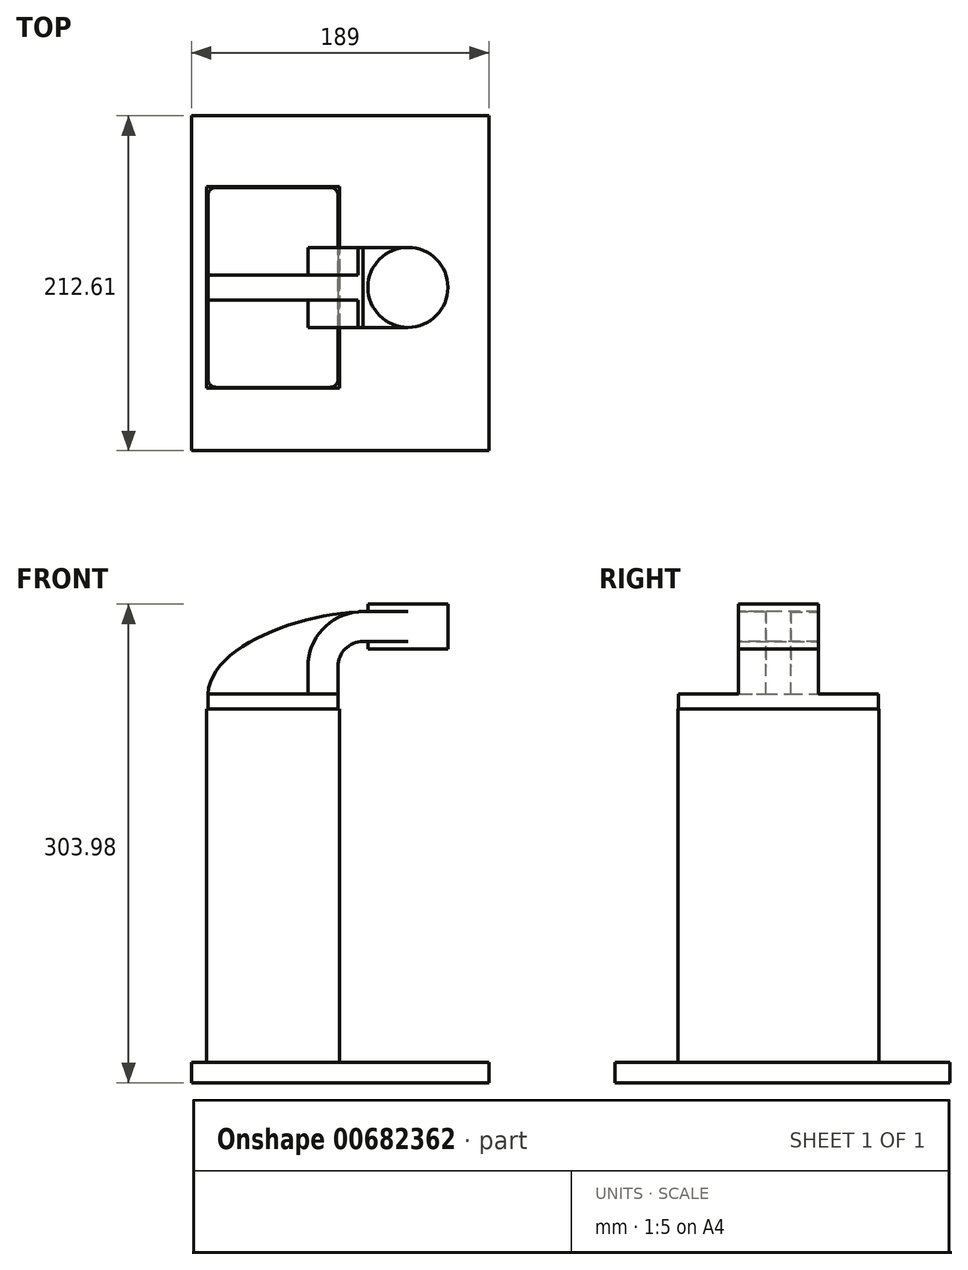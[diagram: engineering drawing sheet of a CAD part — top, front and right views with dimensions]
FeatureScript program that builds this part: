
annotation { "Feature Type Name" : "Feature", "Feature Type Description" : "" }
export const myFeature = defineFeature(function(context is Context, id is Id, definition is map)
    precondition{}
    {
        {
            var Q0;
            Q0=qCreatedBy(makeId("Front.planeOp"),FACE);
            var sketch = newSketch(context, id + "F0", { "sketchPlane" : qUnion([Q0])});
            skLineSegment(sketch, "E0.rect.bottom", {"start": v(-41.28, 9.52) * mm, "end": v(41.28, 9.52) * mm});
            skLineSegment(sketch, "E0.rect.top", {"start": v(-41.28, -9.52) * mm, "end": v(41.28, -9.52) * mm});
            skLineSegment(sketch, "E0.rect.left", {"start": v(-41.28, 9.52) * mm, "end": v(-41.28, -9.52) * mm});
            skLineSegment(sketch, "E0.rect.right", {"start": v(41.28, 9.52) * mm, "end": v(41.28, -9.52) * mm});
            skPoint(sketch, "E0.rect.middle", {"position": v(0, 0) * mm});
            skLineSegment(sketch, "E1", {"start": v(41.28, 9.52) * mm, "end": v(41.28, 27) * mm});
            skArc(sketch, "E2", {"start": v(41.28, 27) * mm, "mid": v(45.92, 38.23) * mm, "end": v(57.15, 42.88) * mm});
            skLineSegment(sketch, "E3", {"start": v(57.15, 42.88) * mm, "end": v(85.72, 42.88) * mm});
            skLineSegment(sketch, "E4.rect.bottom", {"start": v(60.32, 38.1) * mm, "end": v(111.12, 38.1) * mm});
            skLineSegment(sketch, "E4.rect.top", {"start": v(60.32, 66.68) * mm, "end": v(111.12, 66.68) * mm});
            skLineSegment(sketch, "E4.rect.left", {"start": v(60.32, 38.1) * mm, "end": v(60.32, 66.68) * mm});
            skLineSegment(sketch, "E4.rect.right", {"start": v(111.13, 38.1) * mm, "end": v(111.12, 66.68) * mm});
            skPoint(sketch, "E4.rect.middle", {"position": v(85.72, 52.39) * mm});
            skLineSegment(sketch, "E5.0", {"start": v(57.15, 61.93) * mm, "end": v(85.72, 61.93) * mm});
            skArc(sketch, "E5.1", {"start": v(22.23, 27) * mm, "mid": v(32.45, 51.7) * mm, "end": v(57.15, 61.93) * mm});
            skLineSegment(sketch, "E5.2", {"start": v(22.23, 9.52) * mm, "end": v(22.23, 27) * mm});
            skLineSegment(sketch, "E6", {"start": v(85.72, 38.1) * mm, "end": v(85.72, 66.68) * mm});
            skFitSpline(sketch, "E7", {"points": [v(-41.28, 9.53) * mm, v(57.15, 61.93) * mm], "startDerivative": vector(5.2, 92.34) * mm, "endDerivative": vector(120.92, 4.22) * mm});
            skSolve(sketch);
        }
        {
            var Q0;
            Q0=makeQuery(id+"F0.imprint","IMPRINT",FACE,{"disambiguationData":[TD([[makeQuery(id+"F0.imprint","IMPRINT",EDGE,{"derivedFrom":sQuery(id+"F0.wireOp",EDGE,"E0.rect.top")}),1.0]])]});
            extrude(context, id + "F1", {"entities" : qUnion([Q0]), "endBound" : BoundingType.SYMMETRIC, "depth" : 127 * mm});
        }
        {
            var Q0;
            {var subQ9=sQuery(id+"F0.wireOp",EDGE,"E1");Q0=makeQuery(id+"F0.imprint","IMPRINT",FACE,{"disambiguationData":[TD([[makeQuery(id+"F0.imprint","IMPRINT",EDGE,{"derivedFrom":subQ9}),1.0]])]});}
            var Q1;
            {var subQ0=sQuery(id+"F0.wireOp",EDGE,"E6");var subQ1=sQuery(id+"F0.wireOp",EDGE,"E3");var subQ2=makeQuery(id+"F0.imprint","INTERSECT",VERTEX,{"derivedFrom":[subQ1,subQ0]});Q1=makeQuery(id+"F0.imprint","IMPRINT",FACE,{"disambiguationData":[TD([[makeQuery(id+"F0.imprint","IMPRINT",EDGE,{"disambiguationData":[TD([[subQ2,1.0]])],"derivedFrom":subQ1}),1.0]])]});}
            extrude(context, id + "F2", {"entities" : qUnion([Q0, Q1]), "operationType" : NewBodyOperationType.ADD, "endBound" : BoundingType.SYMMETRIC, "depth" : 50.8 * mm});
        }
        {
            var Q0;
            {var subQ3=sQuery(id+"F0.wireOp",EDGE,"E5.2");Q0=makeQuery(id+"F0.imprint","IMPRINT",FACE,{"disambiguationData":[TD([[makeQuery(id+"F0.imprint","IMPRINT",EDGE,{"derivedFrom":subQ3}),1.0]])]});}
            extrude(context, id + "F3", {"entities" : qUnion([Q0]), "operationType" : NewBodyOperationType.ADD, "endBound" : BoundingType.SYMMETRIC, "depth" : 15.88 * mm});
        }
        {
            var Q0;
            {var subQ5=sQuery(id+"F0.wireOp",EDGE,"E4.rect.right");Q0=makeQuery(id+"F0.imprint","IMPRINT",FACE,{"disambiguationData":[TD([[makeQuery(id+"F0.imprint","IMPRINT",EDGE,{"derivedFrom":subQ5}),1.0]])]});}
            var Q1;
            Q1=sQuery(id+"F0.wireOp",EDGE,"E6");
            revolve(context, id + "F4", {"operationType" : NewBodyOperationType.ADD, "entities" : qUnion([Q0]), "axis" : qUnion([Q1]), "revolveType" : RevolveType.FULL});
        }
        {
            var Q0;
            Q0=makeQuery(id+"F1.opExtrude","CAP_EDGE",EDGE,{"disambiguationData":[OSD([sQuery(id+"F0.wireOp",EDGE,"E0.rect.right")])],"isStart":false});
            var Q1;
            Q1=makeQuery(id+"F1.opExtrude","CAP_EDGE",EDGE,{"disambiguationData":[OSD([sQuery(id+"F0.wireOp",EDGE,"E0.rect.left")])],"isStart":false});
            var Q2;
            Q2=makeQuery(id+"F1.opExtrude","CAP_EDGE",EDGE,{"disambiguationData":[OSD([sQuery(id+"F0.wireOp",EDGE,"E0.rect.right")])],"isStart":true});
            var Q3;
            Q3=makeQuery(id+"F1.opExtrude","CAP_EDGE",EDGE,{"disambiguationData":[OSD([sQuery(id+"F0.wireOp",EDGE,"E0.rect.left")])],"isStart":true});
            fillet(context, id + "F5", {"entities" : qUnion([Q0, Q1, Q2, Q3]), "radius" : 5.08 * mm, "tangentPropagation" : true, "allowEdgeOverflow" : false});
        }
        {
            var Q0;
            Q0=qCreatedBy(makeId("Top.planeOp"),FACE);
            var sketch = newSketch(context, id + "F6", { "sketchPlane" : qUnion([Q0])});
            skLineSegment(sketch, "E8.bottom", {"start": v(42.19, -63.88) * mm, "end": v(-42.19, -63.88) * mm});
            skLineSegment(sketch, "E8.top", {"start": v(42.19, 63.88) * mm, "end": v(-42.19, 63.88) * mm});
            skLineSegment(sketch, "E8.left", {"start": v(42.19, -63.88) * mm, "end": v(42.19, 63.88) * mm});
            skLineSegment(sketch, "E8.right", {"start": v(-42.19, -63.88) * mm, "end": v(-42.19, 63.88) * mm});
            skPoint(sketch, "E8.middle", {"position": v(0, 0) * mm});
            skSolve(sketch);
        }
        {
            var Q0;
            Q0 = qSketchRegion(id + "F6", true);
            extrude(context, id + "F7", {"entities" : qUnion([Q0]), "operationType" : NewBodyOperationType.ADD, "oppositeDirection" : true, "depth" : 229.7 * mm, "offsetDistance" : 25.4 * mm});
        }
        {
            var Q0;
            Q0=qCreatedBy(makeId("Right.planeOp"),FACE);
            var sketch = newSketch(context, id + "F8", { "sketchPlane" : qUnion([Q0])});
            skLineSegment(sketch, "E9.bottom", {"start": v(-103.7, -224.55) * mm, "end": v(108.92, -224.55) * mm});
            skLineSegment(sketch, "E9.top", {"start": v(-103.7, -237.3) * mm, "end": v(108.92, -237.3) * mm});
            skLineSegment(sketch, "E9.left", {"start": v(-103.7, -224.55) * mm, "end": v(-103.7, -237.3) * mm});
            skLineSegment(sketch, "E9.right", {"start": v(108.92, -224.55) * mm, "end": v(108.92, -237.3) * mm});
            skSolve(sketch);
        }
        {
            var Q0;
            Q0 = qSketchRegion(id + "F8", true);
            extrude(context, id + "F9", {"entities" : qUnion([Q0]), "operationType" : NewBodyOperationType.ADD, "endBound" : BoundingType.SYMMETRIC, "depth" : 103.4 * mm, "offsetDistance" : 25.4 * mm});
        }
        {
            var Q0;
            Q0=makeQuery(id+"F9.opExtrude","CAP_FACE",FACE,{"disambiguationData":[OSD([sQuery(id+"F8.wireOp",EDGE,"E9.bottom"),sQuery(id+"F8.wireOp",EDGE,"E9.top"),sQuery(id+"F8.wireOp",EDGE,"E9.left"),sQuery(id+"F8.wireOp",EDGE,"E9.right")])],"isStart":false});
            extrude(context, id + "F10", {"entities" : qUnion([Q0]), "operationType" : NewBodyOperationType.ADD, "depth" : 85.6 * mm, "offsetDistance" : 25.4 * mm});
        }
        {
            var Q0;
            Q0=qCreatedBy(makeId("Top.planeOp"),FACE);
            var sketch = newSketch(context, id + "F11", { "sketchPlane" : qUnion([Q0])});
            skLineSegment(sketch, "E10", {"start": v(99.74, 0) * mm, "end": v(81.3, 0) * mm});
            skSolve(sketch);
        }
        {
            var Q0;
            Q0=sQuery(id+"F11.wireOp",EDGE,"E10");
            extrude(context, id + "F12", {"bodyType" : ToolBodyType.SURFACE, "surfaceEntities" : qUnion([Q0]), "endBound" : BoundingType.SYMMETRIC, "depth" : 258.36 * mm, "offsetDistance" : 25.4 * mm});
        }
    });
